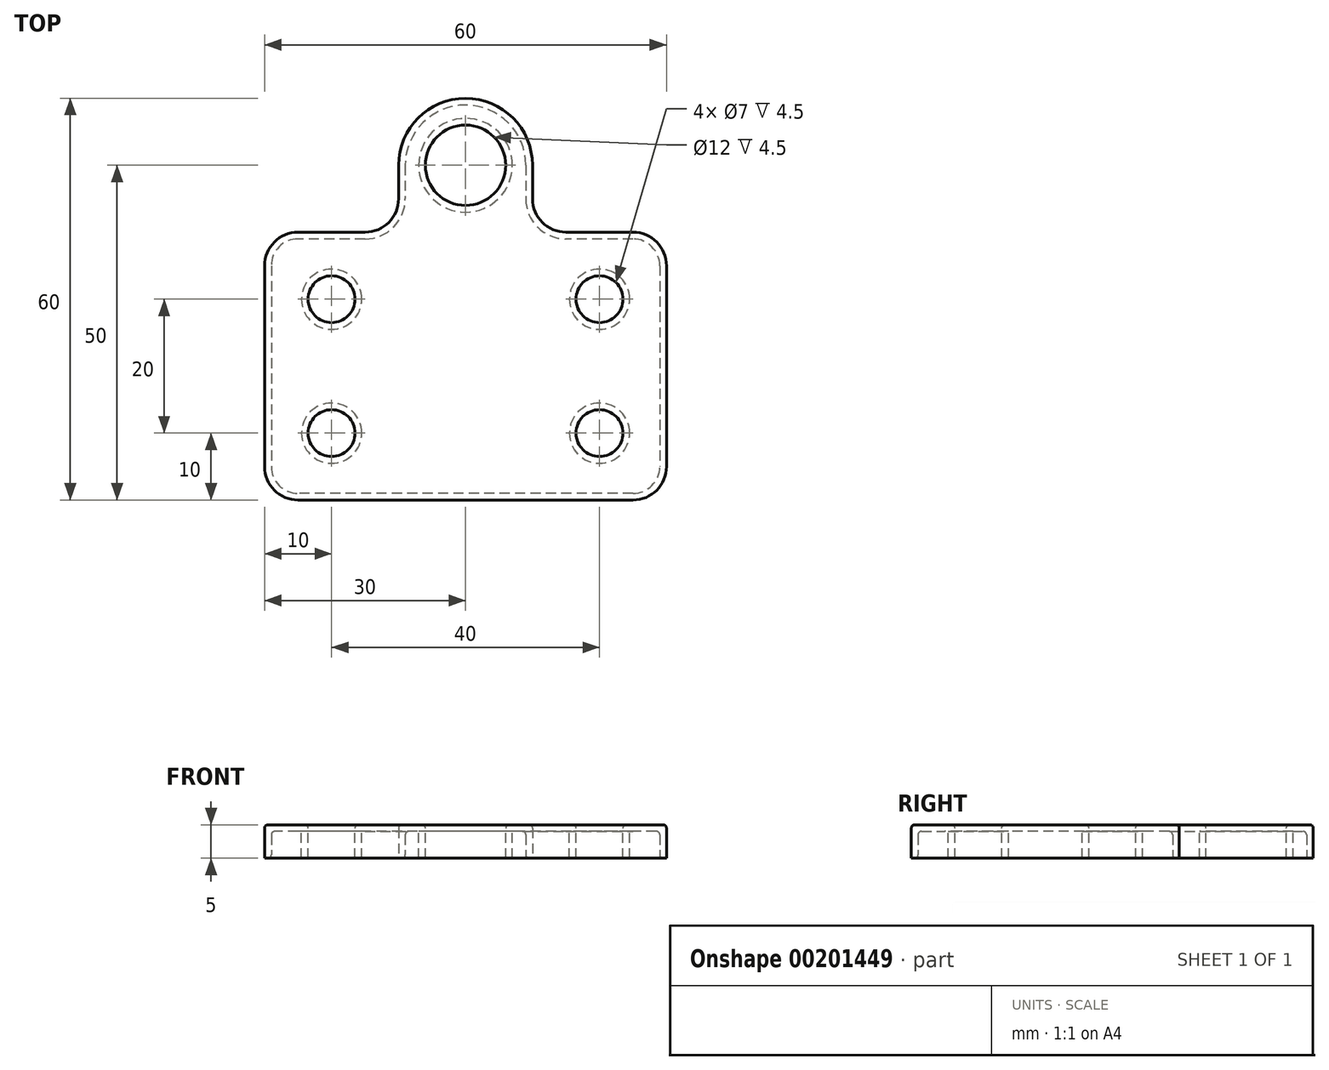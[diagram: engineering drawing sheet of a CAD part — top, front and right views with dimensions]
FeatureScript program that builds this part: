
annotation { "Feature Type Name" : "Feature", "Feature Type Description" : "" }
export const myFeature = defineFeature(function(context is Context, id is Id, definition is map)
    precondition{}
    {
        {
            var Q0;
            Q0=qCreatedBy(makeId("Top.planeOp"),FACE);
            var sketch = newSketch(context, id + "F0", { "sketchPlane" : qUnion([Q0])});
            skLineSegment(sketch, "E0.bottom", {"start": v(30, 20) * mm, "end": v(10, 20) * mm});
            skLineSegment(sketch, "E0.top", {"start": v(30, -20) * mm, "end": v(-30, -20) * mm});
            skLineSegment(sketch, "E0.left", {"start": v(30, 20) * mm, "end": v(30, -20) * mm});
            skLineSegment(sketch, "E0.right", {"start": v(-30, 20) * mm, "end": v(-30, -20) * mm});
            skPoint(sketch, "E0.middle", {"position": v(0, 0) * mm});
            skArc(sketch, "E1", {"start": v(10, 30) * mm, "mid": v(0, 40) * mm, "end": v(-10, 30) * mm});
            skLineSegment(sketch, "E2", {"start": v(10, 30) * mm, "end": v(10, 20) * mm});
            skLineSegment(sketch, "E3", {"start": v(-10, 30) * mm, "end": v(-10, 20) * mm});
            skLineSegment(sketch, "E4.trimOffspring", {"start": v(-10, 20) * mm, "end": v(-30, 20) * mm});
            skSolve(sketch);
        }
        {
            var Q0;
            Q0=makeQuery(id+"F0.imprint","IMPRINT",FACE,{"disambiguationData":[TD([[makeQuery(id+"F0.imprint","IMPRINT",EDGE,{"derivedFrom":sQuery(id+"F0.wireOp",EDGE,"E0.bottom")}),1.0]])]});
            extrude(context, id + "F1", {"entities" : qUnion([Q0]), "depth" : 5 * mm});
        }
        {
            var Q0;
            Q0=makeQuery(id+"F1.opExtrude","SWEPT_EDGE",EDGE,{"disambiguationData":[OSD([sQuery(id+"F0.wireOp",EDGE,"E0.bottom"),sQuery(id+"F0.wireOp",EDGE,"E0.left")])]});
            var Q1;
            Q1=makeQuery(id+"F1.opExtrude","SWEPT_EDGE",EDGE,{"disambiguationData":[OSD([sQuery(id+"F0.wireOp",EDGE,"E0.top"),sQuery(id+"F0.wireOp",EDGE,"E0.left")])]});
            var Q2;
            Q2=makeQuery(id+"F1.opExtrude","SWEPT_EDGE",EDGE,{"disambiguationData":[OSD([sQuery(id+"F0.wireOp",EDGE,"E0.bottom"),sQuery(id+"F0.wireOp",EDGE,"E2")])]});
            var Q3;
            Q3=makeQuery(id+"F1.opExtrude","SWEPT_EDGE",EDGE,{"disambiguationData":[OSD([sQuery(id+"F0.wireOp",EDGE,"E0.top"),sQuery(id+"F0.wireOp",EDGE,"E0.right")])]});
            var Q4;
            Q4=makeQuery(id+"F1.opExtrude","SWEPT_EDGE",EDGE,{"disambiguationData":[OSD([sQuery(id+"F0.wireOp",EDGE,"E0.right"),sQuery(id+"F0.wireOp",EDGE,"E4.trimOffspring")])]});
            var Q5;
            Q5=makeQuery(id+"F1.opExtrude","SWEPT_EDGE",EDGE,{"disambiguationData":[OSD([sQuery(id+"F0.wireOp",EDGE,"E3"),sQuery(id+"F0.wireOp",EDGE,"E4.trimOffspring")])]});
            fillet(context, id + "F2", {"entities" : qUnion([Q0, Q1, Q2, Q3, Q4, Q5]), "radius" : 5 * mm, "tangentPropagation" : true, "allowEdgeOverflow" : false});
        }
        {
            var Q0;
            Q0=makeQuery(id+"F1.opExtrude","CAP_FACE",FACE,{"disambiguationData":[OSD([sQuery(id+"F0.wireOp",EDGE,"E0.bottom"),sQuery(id+"F0.wireOp",EDGE,"E0.top"),sQuery(id+"F0.wireOp",EDGE,"E0.left"),sQuery(id+"F0.wireOp",EDGE,"E0.right"),sQuery(id+"F0.wireOp",EDGE,"E1"),sQuery(id+"F0.wireOp",EDGE,"E2"),sQuery(id+"F0.wireOp",EDGE,"E3"),sQuery(id+"F0.wireOp",EDGE,"E4.trimOffspring")])],"isStart":false});
            var sketch = newSketch(context, id + "F3", { "sketchPlane" : qUnion([Q0])});
            skPoint(sketch, "E5", {"position": v(20, 10) * mm});
            skLineSegment(sketch, "E6", {"start": v(0, 40) * mm, "end": v(0, -20) * mm, "construction": true});
            skLineSegment(sketch, "E7", {"start": v(30, 0) * mm, "end": v(-30, 0) * mm, "construction": true});
            skPoint(sketch, "E8.MirrorP", {"position": v(20, -10) * mm});
            skPoint(sketch, "E9.MirrorP", {"position": v(-20, 10) * mm});
            skPoint(sketch, "E10.MirrorP", {"position": v(-20, -10) * mm});
            skSolve(sketch);
        }
        {
            var Q0;
            Q0=sQuery(id+"F3.wireOp",VERTEX,"E5");
            var Q1;
            Q1=sQuery(id+"F3.wireOp",VERTEX,"E8.MirrorP");
            var Q2;
            Q2=sQuery(id+"F3.wireOp",VERTEX,"E9.MirrorP");
            var Q3;
            Q3=sQuery(id+"F3.wireOp",VERTEX,"E10.MirrorP");
            var Q4;
            Q4=makeQuery(id+"F1.opExtrude","SWEPT_BODY",BODY,{"disambiguationData":[OSD([sQuery(id+"F0.wireOp",EDGE,"E0.bottom"),sQuery(id+"F0.wireOp",EDGE,"E0.top"),sQuery(id+"F0.wireOp",EDGE,"E0.left"),sQuery(id+"F0.wireOp",EDGE,"E0.right"),sQuery(id+"F0.wireOp",EDGE,"E1"),sQuery(id+"F0.wireOp",EDGE,"E2"),sQuery(id+"F0.wireOp",EDGE,"E3"),sQuery(id+"F0.wireOp",EDGE,"E4.trimOffspring")])]});
            hole(context, id + "F4", {"style" : HoleStyle.SIMPLE, "endStyle" : HoleEndStyle.THROUGH, "holeDiameter" : 7 * mm, "locations" : qUnion([Q0, Q1, Q2, Q3]), "scope" : qUnion([Q4]), "isTappedThrough" : true});
        }
        {
            var Q0;
            Q0=makeQuery(id+"F1.opExtrude","CAP_FACE",FACE,{"disambiguationData":[OSD([sQuery(id+"F0.wireOp",EDGE,"E0.bottom"),sQuery(id+"F0.wireOp",EDGE,"E0.top"),sQuery(id+"F0.wireOp",EDGE,"E0.left"),sQuery(id+"F0.wireOp",EDGE,"E0.right"),sQuery(id+"F0.wireOp",EDGE,"E1"),sQuery(id+"F0.wireOp",EDGE,"E2"),sQuery(id+"F0.wireOp",EDGE,"E3"),sQuery(id+"F0.wireOp",EDGE,"E4.trimOffspring")])],"isStart":false});
            var sketch = newSketch(context, id + "F5", { "sketchPlane" : qUnion([Q0])});
            skPoint(sketch, "E11", {"position": v(0, 30) * mm});
            skSolve(sketch);
        }
        {
            var Q0;
            Q0=sQuery(id+"F5.wireOp",VERTEX,"E11");
            var Q1;
            Q1=makeQuery(id+"F1.opExtrude","SWEPT_BODY",BODY,{"disambiguationData":[OSD([sQuery(id+"F0.wireOp",EDGE,"E0.bottom"),sQuery(id+"F0.wireOp",EDGE,"E0.top"),sQuery(id+"F0.wireOp",EDGE,"E0.left"),sQuery(id+"F0.wireOp",EDGE,"E0.right"),sQuery(id+"F0.wireOp",EDGE,"E1"),sQuery(id+"F0.wireOp",EDGE,"E2"),sQuery(id+"F0.wireOp",EDGE,"E3"),sQuery(id+"F0.wireOp",EDGE,"E4.trimOffspring")])]});
            hole(context, id + "F6", {"style" : HoleStyle.SIMPLE, "endStyle" : HoleEndStyle.THROUGH, "holeDiameter" : 12 * mm, "locations" : qUnion([Q0]), "scope" : qUnion([Q1]), "isTappedThrough" : true});
        }
        {
            var Q0;
            Q0=makeQuery(id+"F1.opExtrude","CAP_FACE",FACE,{"disambiguationData":[OSD([sQuery(id+"F0.wireOp",EDGE,"E0.bottom"),sQuery(id+"F0.wireOp",EDGE,"E0.top"),sQuery(id+"F0.wireOp",EDGE,"E0.left"),sQuery(id+"F0.wireOp",EDGE,"E0.right"),sQuery(id+"F0.wireOp",EDGE,"E1"),sQuery(id+"F0.wireOp",EDGE,"E2"),sQuery(id+"F0.wireOp",EDGE,"E3"),sQuery(id+"F0.wireOp",EDGE,"E4.trimOffspring")])],"isStart":false});
            fillet(context, id + "F7", {"entities" : qUnion([Q0]), "radius" : 0.5 * mm, "tangentPropagation" : true, "allowEdgeOverflow" : false});
        }
        {
            var Q0;
            Q0=makeQuery(id+"F1.opExtrude","CAP_FACE",FACE,{"disambiguationData":[OSD([sQuery(id+"F0.wireOp",EDGE,"E0.bottom"),sQuery(id+"F0.wireOp",EDGE,"E0.top"),sQuery(id+"F0.wireOp",EDGE,"E0.left"),sQuery(id+"F0.wireOp",EDGE,"E0.right"),sQuery(id+"F0.wireOp",EDGE,"E1"),sQuery(id+"F0.wireOp",EDGE,"E2"),sQuery(id+"F0.wireOp",EDGE,"E3"),sQuery(id+"F0.wireOp",EDGE,"E4.trimOffspring")])],"isStart":true});
            shell(context, id + "F8", {"entities" : qUnion([Q0]), "thickness" : 1 * mm});
        }
        {
            var Q0;
            {var subQ0=sQuery(id+"F0.wireOp",EDGE,"E4.trimOffspring");var subQ1=sQuery(id+"F0.wireOp",EDGE,"E3");var subQ2=sQuery(id+"F0.wireOp",EDGE,"E2");var subQ3=sQuery(id+"F0.wireOp",EDGE,"E1");var subQ4=sQuery(id+"F0.wireOp",EDGE,"E0.right");var subQ5=sQuery(id+"F0.wireOp",EDGE,"E0.left");var subQ6=sQuery(id+"F0.wireOp",EDGE,"E0.top");var subQ7=sQuery(id+"F0.wireOp",EDGE,"E0.bottom");var subQ8=makeQuery(id+"F1.opExtrude","CAP_EDGE",EDGE,{"disambiguationData":[OSD([subQ4])],"isStart":false});Q0=makeQuery(id+"F8.opShell","OFFSET_EDGE",EDGE,{"disambiguationData":[OSD([subQ7,subQ6,subQ5,subQ4,subQ3,subQ2,subQ1,subQ0]),TDD([makeQuery(id+"F7.opFillet","BLEND_EDGE",EDGE,{"blendedFrom":[subQ8,makeQuery(id+"F1.opExtrude","SWEPT_FACE",FACE,{"disambiguationData":[OSD([subQ4])]})],"blendedInto":[makeQuery(id+"F1.opExtrude","SWEPT_FACE",FACE,{"disambiguationData":[OSD([subQ4])]})]}),makeQuery(id+"F7.opFillet","BLEND_EDGE",EDGE,{"blendedFrom":[subQ8,makeQuery(id+"F1.opExtrude","CAP_FACE",FACE,{"disambiguationData":[OSD([subQ7,subQ6,subQ5,subQ4,subQ3,subQ2,subQ1,subQ0])],"isStart":false})],"blendedInto":[makeQuery(id+"F1.opExtrude","CAP_FACE",FACE,{"disambiguationData":[OSD([subQ7,subQ6,subQ5,subQ4,subQ3,subQ2,subQ1,subQ0])],"isStart":false})]})])]});}
            var Q1;
            Q1=makeQuery(id+"F8.opShell","OFFSET_EDGE",EDGE,{"disambiguationData":[OSD([sQuery(id+"F0.wireOp",EDGE,"E0.bottom"),sQuery(id+"F0.wireOp",EDGE,"E0.top"),sQuery(id+"F0.wireOp",EDGE,"E0.left"),sQuery(id+"F0.wireOp",EDGE,"E0.right"),sQuery(id+"F0.wireOp",EDGE,"E1"),sQuery(id+"F0.wireOp",EDGE,"E2"),sQuery(id+"F0.wireOp",EDGE,"E3"),sQuery(id+"F0.wireOp",EDGE,"E4.trimOffspring"),sQuery(id+"F4.hole-3.sketch.wireOp",EDGE,"core_line_2"),sQuery(id+"F4.hole-3.sketch.wireOp",EDGE,"core_line_3")])]});
            var Q2;
            Q2=makeQuery(id+"F8.opShell","OFFSET_EDGE",EDGE,{"disambiguationData":[OSD([sQuery(id+"F0.wireOp",EDGE,"E0.bottom"),sQuery(id+"F0.wireOp",EDGE,"E0.top"),sQuery(id+"F0.wireOp",EDGE,"E0.left"),sQuery(id+"F0.wireOp",EDGE,"E0.right"),sQuery(id+"F0.wireOp",EDGE,"E1"),sQuery(id+"F0.wireOp",EDGE,"E2"),sQuery(id+"F0.wireOp",EDGE,"E3"),sQuery(id+"F0.wireOp",EDGE,"E4.trimOffspring"),sQuery(id+"F4.hole-1.sketch.wireOp",EDGE,"core_line_2"),sQuery(id+"F4.hole-1.sketch.wireOp",EDGE,"core_line_3")])]});
            var Q3;
            Q3=makeQuery(id+"F8.opShell","OFFSET_EDGE",EDGE,{"disambiguationData":[OSD([sQuery(id+"F0.wireOp",EDGE,"E0.bottom"),sQuery(id+"F0.wireOp",EDGE,"E0.top"),sQuery(id+"F0.wireOp",EDGE,"E0.left"),sQuery(id+"F0.wireOp",EDGE,"E0.right"),sQuery(id+"F0.wireOp",EDGE,"E1"),sQuery(id+"F0.wireOp",EDGE,"E2"),sQuery(id+"F0.wireOp",EDGE,"E3"),sQuery(id+"F0.wireOp",EDGE,"E4.trimOffspring"),sQuery(id+"F4.hole-0.sketch.wireOp",EDGE,"core_line_2"),sQuery(id+"F4.hole-0.sketch.wireOp",EDGE,"core_line_3")])]});
            var Q4;
            Q4=makeQuery(id+"F8.opShell","OFFSET_EDGE",EDGE,{"disambiguationData":[OSD([sQuery(id+"F0.wireOp",EDGE,"E0.bottom"),sQuery(id+"F0.wireOp",EDGE,"E0.top"),sQuery(id+"F0.wireOp",EDGE,"E0.left"),sQuery(id+"F0.wireOp",EDGE,"E0.right"),sQuery(id+"F0.wireOp",EDGE,"E1"),sQuery(id+"F0.wireOp",EDGE,"E2"),sQuery(id+"F0.wireOp",EDGE,"E3"),sQuery(id+"F0.wireOp",EDGE,"E4.trimOffspring"),sQuery(id+"F6.hole-0.sketch.wireOp",EDGE,"core_line_2"),sQuery(id+"F6.hole-0.sketch.wireOp",EDGE,"core_line_3")])]});
            var Q5;
            Q5=makeQuery(id+"F8.opShell","OFFSET_EDGE",EDGE,{"disambiguationData":[OSD([sQuery(id+"F0.wireOp",EDGE,"E0.bottom"),sQuery(id+"F0.wireOp",EDGE,"E0.top"),sQuery(id+"F0.wireOp",EDGE,"E0.left"),sQuery(id+"F0.wireOp",EDGE,"E0.right"),sQuery(id+"F0.wireOp",EDGE,"E1"),sQuery(id+"F0.wireOp",EDGE,"E2"),sQuery(id+"F0.wireOp",EDGE,"E3"),sQuery(id+"F0.wireOp",EDGE,"E4.trimOffspring"),sQuery(id+"F4.hole-2.sketch.wireOp",EDGE,"core_line_2"),sQuery(id+"F4.hole-2.sketch.wireOp",EDGE,"core_line_3")])]});
            fillet(context, id + "F9", {"entities" : qUnion([Q0, Q1, Q2, Q3, Q4, Q5]), "radius" : 0.5 * mm, "tangentPropagation" : true, "allowEdgeOverflow" : false});
        }
    });
